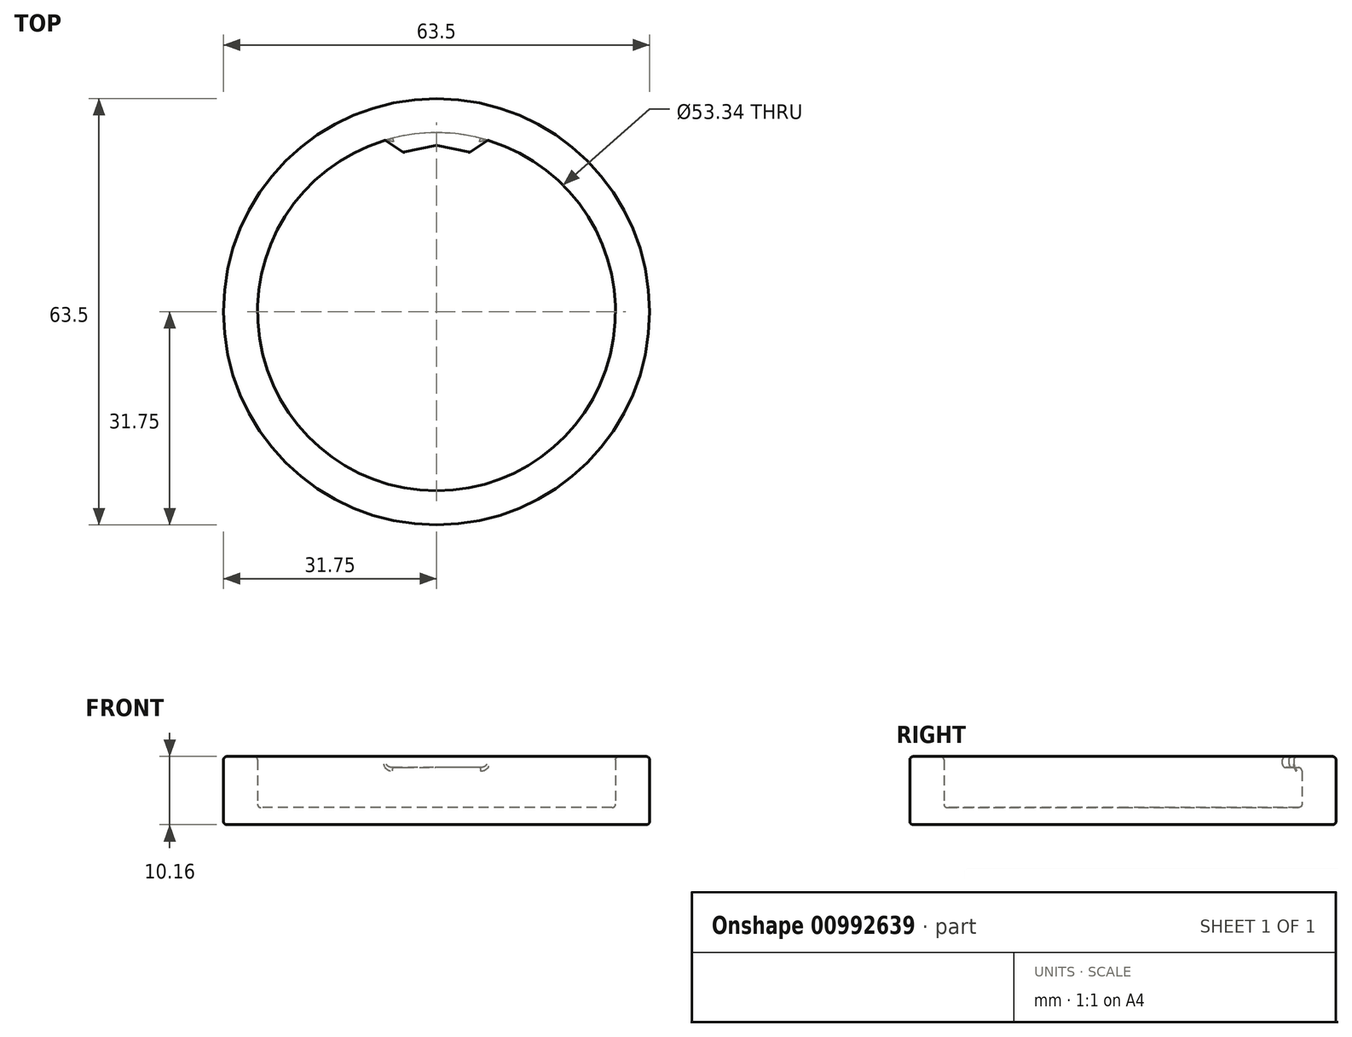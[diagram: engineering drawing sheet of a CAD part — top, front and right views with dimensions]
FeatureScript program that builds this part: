
annotation { "Feature Type Name" : "Feature", "Feature Type Description" : "" }
export const myFeature = defineFeature(function(context is Context, id is Id, definition is map)
    precondition{}
    {
        {
            var Q0;
            Q0=qCreatedBy(makeId("Top.planeOp"),FACE);
            var sketch = newSketch(context, id + "F0", { "sketchPlane" : qUnion([Q0])});
            skCircle(sketch, "E0", {"center": v(0, 0) * mm, "radius": 31.75 * mm});
            skSolve(sketch);
        }
        {
            var Q0;
            Q0 = qSketchRegion(id + "F0", true);
            extrude(context, id + "F1", {"entities" : qUnion([Q0]), "depth" : 2.54 * mm, "offsetDistance" : 25.4 * mm});
        }
        {
            var Q0;
            Q0=makeQuery(id+"F1.opExtrude","CAP_FACE",FACE,{"disambiguationData":[OSD([sQuery(id+"F0.wireOp",EDGE,"E0")])],"isStart":false});
            var sketch = newSketch(context, id + "F2", { "sketchPlane" : qUnion([Q0])});
            skCircle(sketch, "E1", {"center": v(0, 0) * mm, "radius": 26.67 * mm});
            skCircle(sketch, "E2", {"center": v(0, 0) * mm, "radius": 31.75 * mm});
            skSolve(sketch);
        }
        {
            var Q0;
            Q0 = qSketchRegion(id + "F2", true);
            extrude(context, id + "F3", {"entities" : qUnion([Q0]), "operationType" : NewBodyOperationType.ADD, "depth" : 7.62 * mm, "offsetDistance" : 25.4 * mm});
        }
        {
            var Q0;
            Q0=makeQuery(id+"F3.opExtrude","CAP_FACE",FACE,{"disambiguationData":[OSD([sQuery(id+"F2.wireOp",EDGE,"E1"),sQuery(id+"F2.wireOp",EDGE,"E2")])],"isStart":false});
            var sketch = newSketch(context, id + "F4", { "sketchPlane" : qUnion([Q0])});
            skLineSegment(sketch, "E3", {"start": v(-7.62, 25.56) * mm, "end": v(-4.97, 23.74) * mm});
            skLineSegment(sketch, "E4", {"start": v(-4.97, 23.74) * mm, "end": v(0, 24.78) * mm});
            skLineSegment(sketch, "E5", {"start": v(0, 24.78) * mm, "end": v(0, 31.75) * mm});
            skLineSegment(sketch, "E6", {"start": v(0, 31.75) * mm, "end": v(-7.62, 25.56) * mm});
            skLineSegment(sketch, "E7.MirrorCS", {"start": v(4.97, 23.74) * mm, "end": v(0, 24.78) * mm});
            skLineSegment(sketch, "E8.MirrorCS", {"start": v(7.62, 25.56) * mm, "end": v(4.97, 23.74) * mm});
            skLineSegment(sketch, "E9.MirrorCS", {"start": v(0, 31.75) * mm, "end": v(7.62, 25.56) * mm});
            skSolve(sketch);
        }
        {
            var Q0;
            Q0 = qSketchRegion(id + "F4", true);
            extrude(context, id + "F5", {"entities" : qUnion([Q0]), "operationType" : NewBodyOperationType.ADD, "oppositeDirection" : true, "depth" : 1.65 * mm, "offsetDistance" : 25.4 * mm});
        }
        {
            var Q0;
            {var subQ0=sQuery(id+"F4.wireOp",EDGE,"E3");var subQ1=sQuery(id+"F2.wireOp",EDGE,"E1");Q0=makeQuery(id+"FKU0xjmdOpNs4vI_1.1.F5.boolean.opBoolean","SPLIT",EDGE,{"disambiguationData":[TD([makeQuery(id+"F5.opExtrude","SWEPT_FACE",FACE,{"disambiguationData":[OSD([subQ0])]})])],"derivedFrom":makeQuery(id+"F3.opExtrude","CAP_EDGE",EDGE,{"disambiguationData":[OSD([subQ1])],"isStart":false})});}
            var Q1;
            {var subQ0=sQuery(id+"F4.wireOp",EDGE,"E9.MirrorCS");var subQ1=sQuery(id+"F4.wireOp",EDGE,"E8.MirrorCS");var subQ2=sQuery(id+"F4.wireOp",EDGE,"E7.MirrorCS");var subQ3=sQuery(id+"F4.wireOp",EDGE,"E6");var subQ4=sQuery(id+"F4.wireOp",EDGE,"E4");var subQ5=sQuery(id+"F4.wireOp",EDGE,"E3");Q1=makeQuery(id+"FKU0xjmdOpNs4vI_1.1.F5.boolean.opBoolean","MERGE",FACE,{"derivedFrom":[makeQuery(id+"F5.boolean.opBoolean","MERGE",FACE,{"derivedFrom":[makeQuery(id+"F3.opExtrude","CAP_FACE",FACE,{"disambiguationData":[OSD([sQuery(id+"F2.wireOp",EDGE,"E1"),sQuery(id+"F2.wireOp",EDGE,"E2")])],"isStart":false}),makeQuery(id+"F5.opExtrude","CAP_FACE",FACE,{"disambiguationData":[OSD([subQ5,subQ4,subQ3,subQ2,subQ1,subQ0])],"isStart":true})]}),makeQuery(id+"FKU0xjmdOpNs4vI_1.1.F5.opExtrude","CAP_FACE",FACE,{"disambiguationData":[OSD([subQ5,subQ4,subQ3,subQ2,subQ1,subQ0])],"isStart":true})]});}
            var Q2;
            Q2=makeQuery(id+"F3.opExtrude","SWEPT_FACE",FACE,{"disambiguationData":[OSD([sQuery(id+"F2.wireOp",EDGE,"E1")])]});
            var Q3;
            Q3=makeQuery(id+"F3.boolean.opBoolean","MERGE",FACE,{"derivedFrom":[makeQuery(id+"F1.opExtrude","SWEPT_FACE",FACE,{"disambiguationData":[OSD([sQuery(id+"F0.wireOp",EDGE,"E0")])]}),makeQuery(id+"F3.opExtrude","SWEPT_FACE",FACE,{"disambiguationData":[OSD([sQuery(id+"F2.wireOp",EDGE,"E2")])]})]});
            var Q4;
            Q4=makeQuery(id+"F5.opExtrude","SWEPT_FACE",FACE,{"disambiguationData":[OSD([sQuery(id+"F4.wireOp",EDGE,"E7.MirrorCS")])]});
            var Q5;
            Q5=makeQuery(id+"F5.opExtrude","SWEPT_FACE",FACE,{"disambiguationData":[OSD([sQuery(id+"F4.wireOp",EDGE,"E4")])]});
            var Q6;
            Q6=makeQuery(id+"F5.opExtrude","SWEPT_FACE",FACE,{"disambiguationData":[OSD([sQuery(id+"F4.wireOp",EDGE,"E8.MirrorCS")])]});
            var Q7;
            Q7=makeQuery(id+"F5.opExtrude","SWEPT_FACE",FACE,{"disambiguationData":[OSD([sQuery(id+"F4.wireOp",EDGE,"E3")])]});
            var Q8;
            Q8=makeQuery(id+"FKU0xjmdOpNs4vI_1.1.F5.opExtrude","SWEPT_FACE",FACE,{"disambiguationData":[OSD([sQuery(id+"F4.wireOp",EDGE,"E7.MirrorCS")])]});
            var Q9;
            Q9=makeQuery(id+"FKU0xjmdOpNs4vI_1.1.F5.opExtrude","SWEPT_FACE",FACE,{"disambiguationData":[OSD([sQuery(id+"F4.wireOp",EDGE,"E8.MirrorCS")])]});
            var Q10;
            Q10=makeQuery(id+"FKU0xjmdOpNs4vI_1.1.F5.opExtrude","SWEPT_FACE",FACE,{"disambiguationData":[OSD([sQuery(id+"F4.wireOp",EDGE,"E4")])]});
            var Q11;
            Q11=makeQuery(id+"FKU0xjmdOpNs4vI_1.1.F5.opExtrude","SWEPT_FACE",FACE,{"disambiguationData":[OSD([sQuery(id+"F4.wireOp",EDGE,"E3")])]});
            fillet(context, id + "F6", {"entities" : qUnion([Q0, Q1, Q2, Q3, Q4, Q5, Q6, Q7, Q8, Q9, Q10, Q11]), "radius" : 0.5 * mm, "tangentPropagation" : true, "allowEdgeOverflow" : false});
        }
    });
